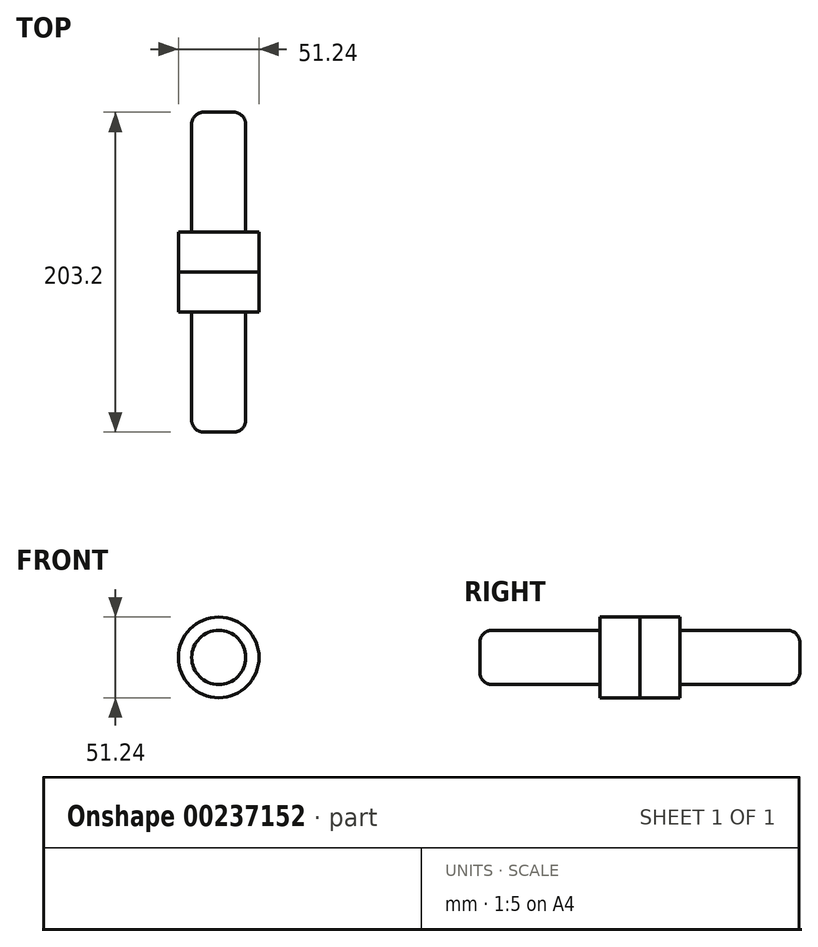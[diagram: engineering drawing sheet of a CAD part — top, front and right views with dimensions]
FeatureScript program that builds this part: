
annotation { "Feature Type Name" : "Feature", "Feature Type Description" : "" }
export const myFeature = defineFeature(function(context is Context, id is Id, definition is map)
    precondition{}
    {
        {
            var Q0;
            Q0=qCreatedBy(makeId("Front.planeOp"),FACE);
            var sketch = newSketch(context, id + "F0", { "sketchPlane" : qUnion([Q0])});
            skCircle(sketch, "E0", {"center": v(0, 0) * mm, "radius": 25.62 * mm});
            skSolve(sketch);
        }
        {
            var Q0;
            Q0=makeQuery(id+"F0.imprint","IMPRINT",FACE,{"disambiguationData":[TD([[makeQuery(id+"F0.imprint","IMPRINT",EDGE,{"derivedFrom":sQuery(id+"F0.wireOp",EDGE,"E0")}),1.0]])]});
            extrude(context, id + "F1", {"entities" : qUnion([Q0]), "depth" : 25.4 * mm});
        }
        {
            var Q0;
            Q0=makeQuery(id+"F1.opExtrude","CAP_FACE",FACE,{"disambiguationData":[OSD([sQuery(id+"F0.wireOp",EDGE,"E0")])],"isStart":false});
            var sketch = newSketch(context, id + "F2", { "sketchPlane" : qUnion([Q0])});
            skCircle(sketch, "E1", {"center": v(0, 0) * mm, "radius": 17.17 * mm});
            skSolve(sketch);
        }
        {
            var Q0;
            Q0=makeQuery(id+"F2.imprint","IMPRINT",FACE,{"disambiguationData":[TD([[makeQuery(id+"F2.imprint","IMPRINT",EDGE,{"derivedFrom":sQuery(id+"F2.wireOp",EDGE,"E1")}),1.0]])]});
            extrude(context, id + "F3", {"entities" : qUnion([Q0]), "operationType" : NewBodyOperationType.ADD, "depth" : 76.2 * mm});
        }
        {
            var Q0;
            Q0=makeQuery(id+"F3.opExtrude","CAP_EDGE",EDGE,{"disambiguationData":[OSD([sQuery(id+"F2.wireOp",EDGE,"E1")])],"isStart":false});
            fillet(context, id + "F4", {"entities" : qUnion([Q0]), "radius" : 7.62 * mm, "tangentPropagation" : true, "allowEdgeOverflow" : false});
        }
        {
            var Q0;
            Q0=makeQuery(id+"F1.opExtrude","SWEPT_BODY",BODY,{"disambiguationData":[OSD([sQuery(id+"F0.wireOp",EDGE,"E0")])]});
            var Q1;
            Q1=qCreatedBy(makeId("Front.planeOp"),FACE);
            mirror(context, id + "F5", {"entities" : qUnion([Q0]), "mirrorPlane" : qUnion([Q1])});
        }
    });
